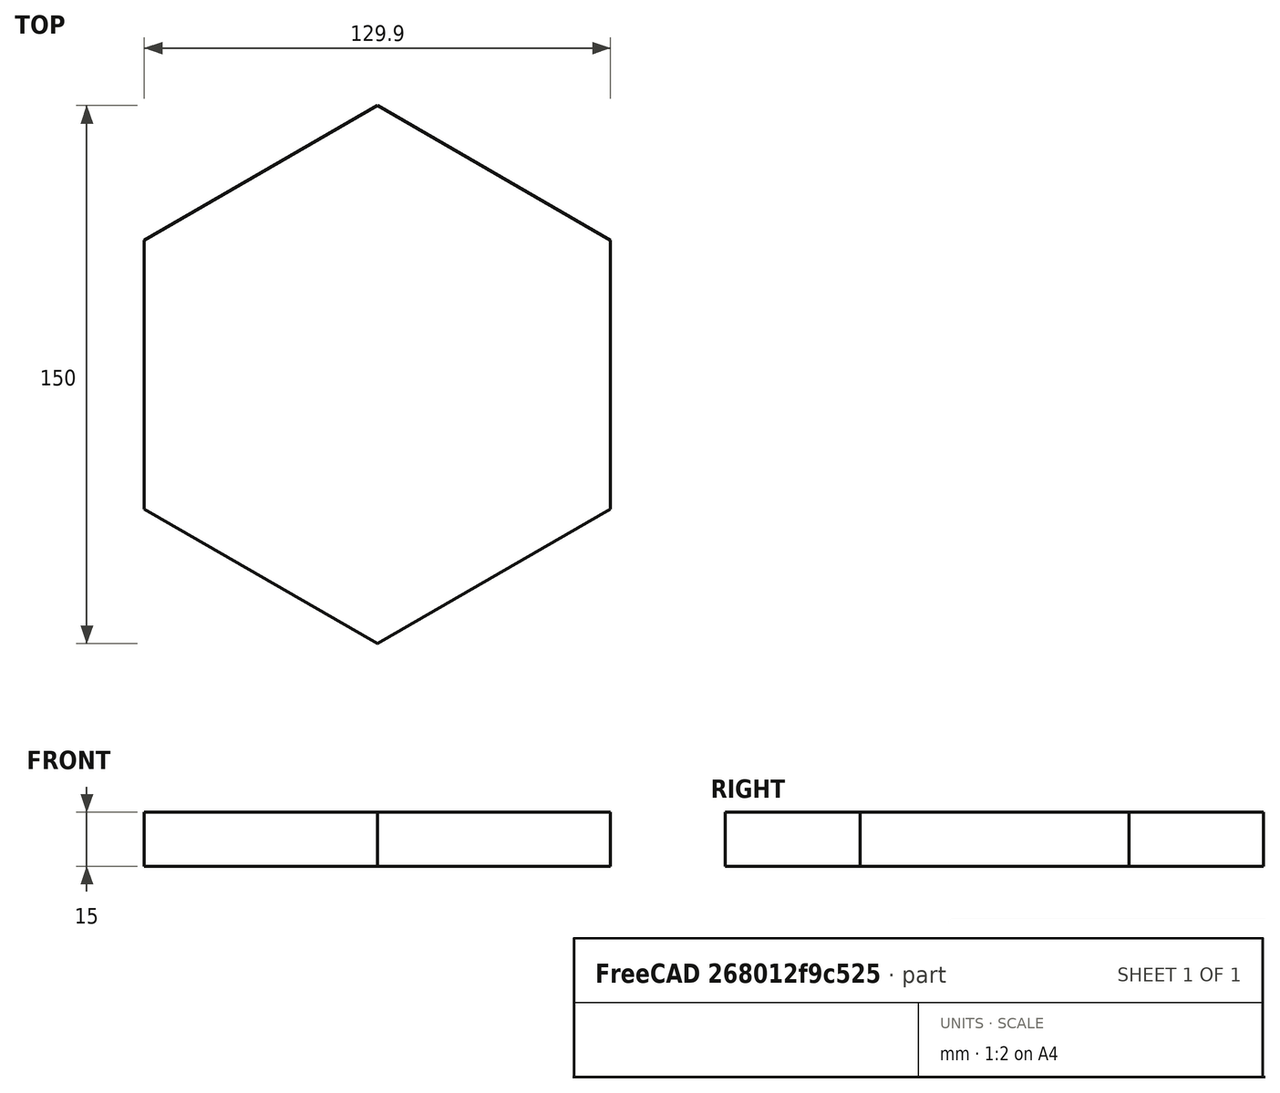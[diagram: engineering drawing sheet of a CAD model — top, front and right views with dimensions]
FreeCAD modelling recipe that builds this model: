
FCSTD DOCUMENT  (FreeCAD 0.19R24291 (Git))
Label: echantillon
License: All rights reserved
LicenseURL: http://en.wikipedia.org/wiki/All_rights_reserved
objects: Sketcher::SketchObject×1, PartDesign::Pad×1, PartDesign::Body×1
note: 4 computed .brp shape members not serialized (recipe doc carries the construction recipe); baked Part::Feature solids carry a one-line shape summary decoded from their .brp

FEATURE [Sketcher::SketchObject] Sketch
  FullyConstrained = true
  MapMode = 5
  Support = -> [XY_Plane]
  sketch-geometry (7):
    g0: LineSegment StartX=64.9519 StartY=37.5 StartZ=0 EndX=0 EndY=75 EndZ=0
    g1: LineSegment StartX=0 StartY=75 StartZ=0 EndX=-64.9519 EndY=37.5 EndZ=0
    g2: LineSegment StartX=-64.9519 StartY=37.5 StartZ=0 EndX=-64.9519 EndY=-37.5 EndZ=0
    g3: LineSegment StartX=-64.9519 StartY=-37.5 StartZ=0 EndX=-2.84e-14 EndY=-75 EndZ=0
    g4: LineSegment StartX=-2.9e-14 StartY=-75 StartZ=0 EndX=64.9519 EndY=-37.5 EndZ=0
    g5: LineSegment StartX=64.9519 StartY=-37.5 StartZ=0 EndX=64.9519 EndY=37.5 EndZ=0
    g6: Circle CenterX=0 CenterY=0 CenterZ=0 NormalX=0 NormalY=0 NormalZ=1 AngleXU=0 Radius=75
  constraints (16):
    c: Coincident(g0,g1)
    c: Coincident(g1,g2)
    c: Coincident(g2,g3)
    c: Coincident(g3,g4)
    c: Coincident(g4,g5)
    c: Coincident(g5,g0)
    c: Equal(g0, g1-g5) x5
    c: PointOnObject(g0,g6)
    c: PointOnObject(g1,g6)
    c: PointOnObject(g2,g6)
    c: PointOnObject(g3,g6)
    c: PointOnObject(g4,g6)
    c: PointOnObject(g5,g6)
    c: Coincident(g6,g-1)
    c: Diameter(g6) = 150
    c: PointOnObject(g0,g-2)
FEATURE [PartDesign::Pad] Pad
  Direction = (1,1,1)
  Length = 15
  Length2 = 100
  Profile = -> Sketch
  Type = 0
FEATURE [PartDesign::Body] Body
  Group = -> [Sketch,Pad]
  Origin = -> Origin
  Tip = -> Pad
